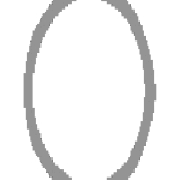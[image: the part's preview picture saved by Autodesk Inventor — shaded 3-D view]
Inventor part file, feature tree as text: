
AUTODESK INVENTOR PART (.ipt)
format: ipt  version: 2021 (Build 250183000, 183)  size: 111,616 bytes
history: native  units: in
note: dims shown in document units (in); Inventor stores cm internally (conversion verified against a paired STEP export)
features: other x4, sketch x3, plane x1
ambient origin geometry x8: Origin, YZ Plane, XZ Plane, XY Plane, X Axis, Y Axis, Z Axis, Center Point
bodies: Solid1 (feature_tree), Body (feature_tree)
feature tree (8):
  other  "Driven Length"
  other  "Frame Generator"
  other  "Start Plane"
  other  "End Plane"
  sketch  "Sketch"  dims[d2=25.5539in d4=-0.0in d5=25.5539in d6=0.12in d7=0.0in d8=90.0deg d9=25.5539in]
  sketch  "Sketch2"  dims[d0=1.0in]
  plane  "Work Plane3"
  sketch  "Sketch3"  dims[d1=0.065in]
